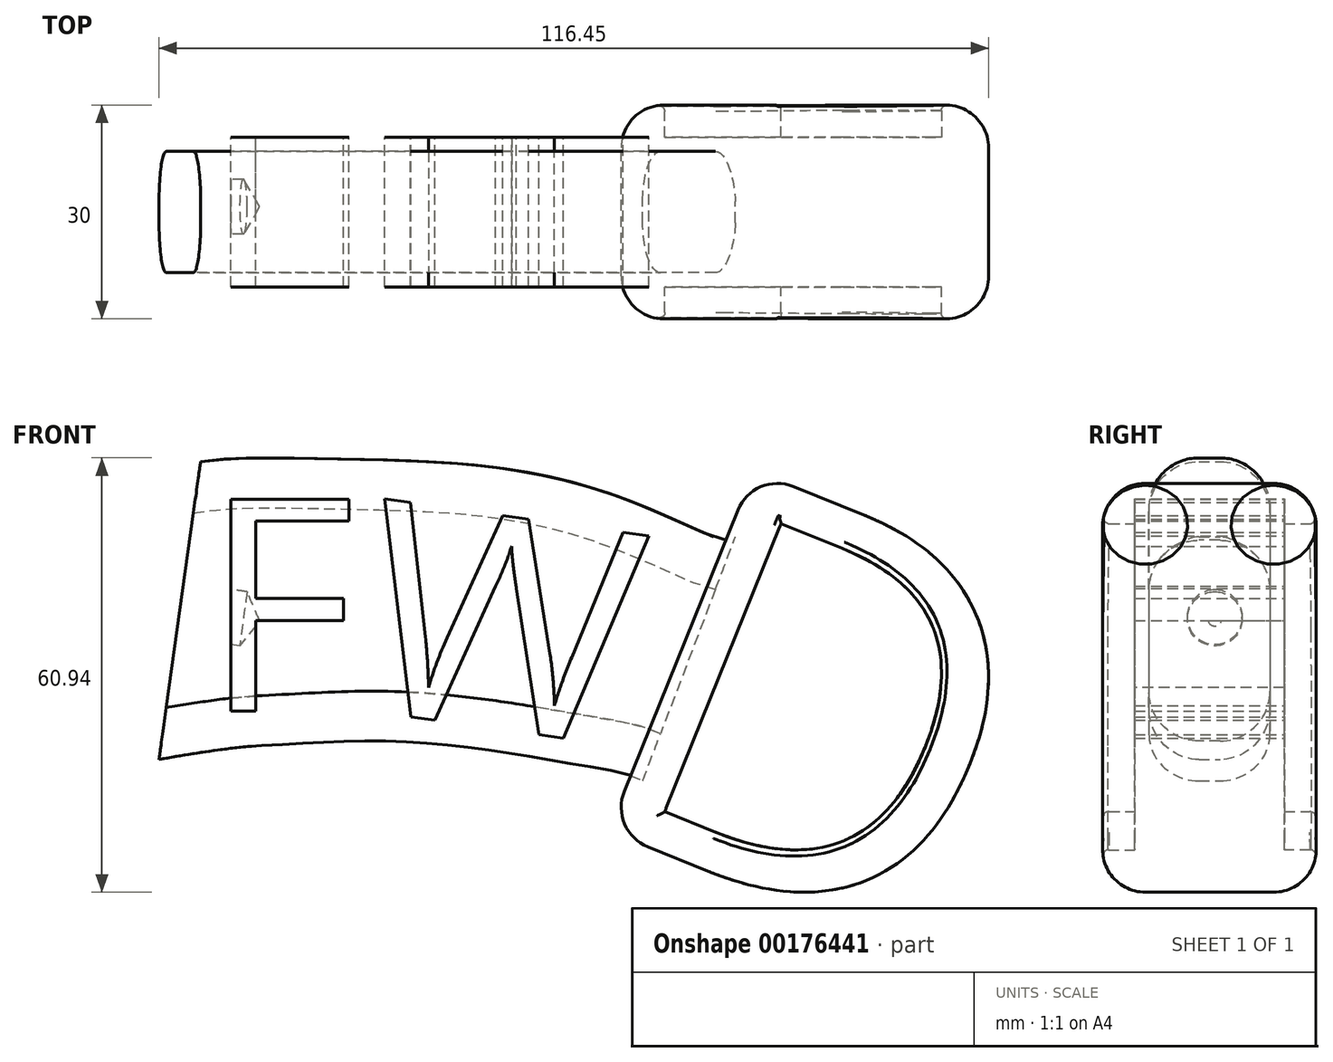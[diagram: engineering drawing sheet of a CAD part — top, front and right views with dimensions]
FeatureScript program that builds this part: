
annotation { "Feature Type Name" : "Feature", "Feature Type Description" : "" }
export const myFeature = defineFeature(function(context is Context, id is Id, definition is map)
    precondition{}
    {
        {
            var Q0;
            Q0=qCreatedBy(makeId("Front.planeOp"),FACE);
            var sketch = newSketch(context, id + "F0", { "sketchPlane" : qUnion([Q0])});
            skText(sketch, "E0", { "text": "F", "fontName": "OpenSans-Regular.ttf"});
            skText(sketch, "E1", { "text": "D", "fontName": "OpenSans-Regular.ttf"});
            skLineSegment(sketch, "E2", {"start": v(0, 30) * mm, "end": v(0, 0) * mm});
            skText(sketch, "E3", { "text": "W", "fontName": "OpenSans-Regular.ttf"});
            const initialGuessF0  = {"E0": [0, 0, 1, 0, 0.03], "E1": [0.08306, -0.01421, 1, 0, 0.055], "E3": [0.03928, 0, 1, 0, 0.03]};
            skSetInitialGuess(sketch, initialGuessF0);
            skSolve(sketch);
        }
        {
            var Q0;
            Q0=makeQuery(id+"F0.imprint","IMPRINT",FACE,{"disambiguationData":[TD([[makeQuery(id+"F0.imprint","IMPRINT",EDGE,{"derivedFrom":sQuery(id+"F0.wireOp",EDGE,"E3.sketch_text.stroke-0")}),-1.0]])]});
            var Q1;
            Q1=makeQuery(id+"F0.imprint","IMPRINT",FACE,{"disambiguationData":[TD([[makeQuery(id+"F0.imprint","IMPRINT",EDGE,{"derivedFrom":sQuery(id+"F0.wireOp",EDGE,"E0.sketch_text.stroke-0")}),-1.0]])]});
            extrude(context, id + "F1", {"entities" : qUnion([Q0, Q1]), "endBound" : BoundingType.SYMMETRIC, "depth" : 21 * mm});
        }
        {
            var Q0;
            Q0=makeQuery(id+"F0.imprint","IMPRINT",FACE,{"disambiguationData":[TD([[makeQuery(id+"F0.imprint","IMPRINT",EDGE,{"derivedFrom":sQuery(id+"F0.wireOp",EDGE,"E1.sketch_text.stroke-0")}),-1.0]])]});
            extrude(context, id + "F2", {"entities" : qUnion([Q0]), "endBound" : BoundingType.SYMMETRIC, "depth" : 30 * mm});
        }
        {
            var Q0;
            Q0=makeQuery(id+"F0.imprint","IMPRINT",FACE,{"disambiguationData":[TD([[makeQuery(id+"F0.imprint","IMPRINT",EDGE,{"derivedFrom":sQuery(id+"F0.wireOp",EDGE,"E1.sketch_text.stroke-7")}),1.0]])]});
            extrude(context, id + "F3", {"entities" : qUnion([Q0]), "operationType" : NewBodyOperationType.ADD, "endBound" : BoundingType.SYMMETRIC, "depth" : 21 * mm});
        }
        {
            var Q0;
            Q0=makeQuery(id+"F1.opExtrude","SWEPT_BODY",BODY,{"disambiguationData":[OSD([sQuery(id+"F0.wireOp",EDGE,"E3.sketch_text.stroke-0"),sQuery(id+"F0.wireOp",EDGE,"E3.sketch_text.stroke-1"),sQuery(id+"F0.wireOp",EDGE,"E3.sketch_text.stroke-2"),sQuery(id+"F0.wireOp",EDGE,"E3.sketch_text.stroke-3"),sQuery(id+"F0.wireOp",EDGE,"E3.sketch_text.stroke-4"),sQuery(id+"F0.wireOp",EDGE,"E3.sketch_text.stroke-5"),sQuery(id+"F0.wireOp",EDGE,"E3.sketch_text.stroke-6"),sQuery(id+"F0.wireOp",EDGE,"E3.sketch_text.stroke-7"),sQuery(id+"F0.wireOp",EDGE,"E3.sketch_text.stroke-8"),sQuery(id+"F0.wireOp",EDGE,"E3.sketch_text.stroke-9"),sQuery(id+"F0.wireOp",EDGE,"E3.sketch_text.stroke-10"),sQuery(id+"F0.wireOp",EDGE,"E3.sketch_text.stroke-11"),sQuery(id+"F0.wireOp",EDGE,"E3.sketch_text.stroke-12"),sQuery(id+"F0.wireOp",EDGE,"E3.sketch_text.stroke-13"),sQuery(id+"F0.wireOp",EDGE,"E3.sketch_text.stroke-14"),sQuery(id+"F0.wireOp",EDGE,"E3.sketch_text.stroke-15"),sQuery(id+"F0.wireOp",EDGE,"E3.sketch_text.stroke-16"),sQuery(id+"F0.wireOp",EDGE,"E3.sketch_text.stroke-17"),sQuery(id+"F0.wireOp",EDGE,"E3.sketch_text.stroke-18"),sQuery(id+"F0.wireOp",EDGE,"E3.sketch_text.stroke-19")])]});
            var Q1;
            Q1=makeQuery(id+"F1.opExtrude","SWEPT_EDGE",EDGE,{"disambiguationData":[OSD([sQuery(id+"F0.wireOp",EDGE,"E3.sketch_text.stroke-6"),sQuery(id+"F0.wireOp",EDGE,"E3.sketch_text.stroke-7")])]});
            transform(context, id + "F4", {"entities" : qUnion([Q0]), "transformType" : TransformType.ROTATION, "transformAxis" : qUnion([Q1]), "angle" : 8 * degree, "makeCopy" : false});
        }
        {
            var Q0;
            Q0=makeQuery(id+"F2.opExtrude","SWEPT_BODY",BODY,{"disambiguationData":[OSD([sQuery(id+"F0.wireOp",EDGE,"E1.sketch_text.stroke-0"),sQuery(id+"F0.wireOp",EDGE,"E1.sketch_text.stroke-1"),sQuery(id+"F0.wireOp",EDGE,"E1.sketch_text.stroke-2"),sQuery(id+"F0.wireOp",EDGE,"E1.sketch_text.stroke-3"),sQuery(id+"F0.wireOp",EDGE,"E1.sketch_text.stroke-4"),sQuery(id+"F0.wireOp",EDGE,"E1.sketch_text.stroke-5"),sQuery(id+"F0.wireOp",EDGE,"E1.sketch_text.stroke-6"),sQuery(id+"F0.wireOp",EDGE,"E1.sketch_text.stroke-7"),sQuery(id+"F0.wireOp",EDGE,"E1.sketch_text.stroke-8"),sQuery(id+"F0.wireOp",EDGE,"E1.sketch_text.stroke-9"),sQuery(id+"F0.wireOp",EDGE,"E1.sketch_text.stroke-10"),sQuery(id+"F0.wireOp",EDGE,"E1.sketch_text.stroke-11"),sQuery(id+"F0.wireOp",EDGE,"E1.sketch_text.stroke-12"),sQuery(id+"F0.wireOp",EDGE,"E1.sketch_text.stroke-13")])]});
            var Q1;
            Q1=makeQuery(id+"F2.opExtrude","SWEPT_EDGE",EDGE,{"disambiguationData":[OSD([sQuery(id+"F0.wireOp",EDGE,"E1.sketch_text.stroke-2"),sQuery(id+"F0.wireOp",EDGE,"E1.sketch_text.stroke-3")])]});
            transform(context, id + "F5", {"entities" : qUnion([Q0]), "transformType" : TransformType.ROTATION, "transformAxis" : qUnion([Q1]), "angle" : 22 * degree, "makeCopy" : false});
        }
        {
            var Q0;
            Q0=makeQuery(id+"F1.opExtrude","SWEPT_BODY",BODY,{"disambiguationData":[OSD([sQuery(id+"F0.wireOp",EDGE,"E3.sketch_text.stroke-0"),sQuery(id+"F0.wireOp",EDGE,"E3.sketch_text.stroke-1"),sQuery(id+"F0.wireOp",EDGE,"E3.sketch_text.stroke-2"),sQuery(id+"F0.wireOp",EDGE,"E3.sketch_text.stroke-3"),sQuery(id+"F0.wireOp",EDGE,"E3.sketch_text.stroke-4"),sQuery(id+"F0.wireOp",EDGE,"E3.sketch_text.stroke-5"),sQuery(id+"F0.wireOp",EDGE,"E3.sketch_text.stroke-6"),sQuery(id+"F0.wireOp",EDGE,"E3.sketch_text.stroke-7"),sQuery(id+"F0.wireOp",EDGE,"E3.sketch_text.stroke-8"),sQuery(id+"F0.wireOp",EDGE,"E3.sketch_text.stroke-9"),sQuery(id+"F0.wireOp",EDGE,"E3.sketch_text.stroke-10"),sQuery(id+"F0.wireOp",EDGE,"E3.sketch_text.stroke-11"),sQuery(id+"F0.wireOp",EDGE,"E3.sketch_text.stroke-12"),sQuery(id+"F0.wireOp",EDGE,"E3.sketch_text.stroke-13"),sQuery(id+"F0.wireOp",EDGE,"E3.sketch_text.stroke-14"),sQuery(id+"F0.wireOp",EDGE,"E3.sketch_text.stroke-15"),sQuery(id+"F0.wireOp",EDGE,"E3.sketch_text.stroke-16"),sQuery(id+"F0.wireOp",EDGE,"E3.sketch_text.stroke-17"),sQuery(id+"F0.wireOp",EDGE,"E3.sketch_text.stroke-18"),sQuery(id+"F0.wireOp",EDGE,"E3.sketch_text.stroke-19")])]});
            transform(context, id + "F6", {"entities" : qUnion([Q0]), "transformType" : TransformType.TRANSLATION_3D, "dx" : -18.4 * mm, "dy" : 0 * mm, "dz" : -0.8 * mm, "makeCopy" : false});
        }
        {
            var Q0;
            Q0=makeQuery(id+"F2.opExtrude","SWEPT_BODY",BODY,{"disambiguationData":[OSD([sQuery(id+"F0.wireOp",EDGE,"E1.sketch_text.stroke-0"),sQuery(id+"F0.wireOp",EDGE,"E1.sketch_text.stroke-1"),sQuery(id+"F0.wireOp",EDGE,"E1.sketch_text.stroke-2"),sQuery(id+"F0.wireOp",EDGE,"E1.sketch_text.stroke-3"),sQuery(id+"F0.wireOp",EDGE,"E1.sketch_text.stroke-4"),sQuery(id+"F0.wireOp",EDGE,"E1.sketch_text.stroke-5"),sQuery(id+"F0.wireOp",EDGE,"E1.sketch_text.stroke-6"),sQuery(id+"F0.wireOp",EDGE,"E1.sketch_text.stroke-7"),sQuery(id+"F0.wireOp",EDGE,"E1.sketch_text.stroke-8"),sQuery(id+"F0.wireOp",EDGE,"E1.sketch_text.stroke-9"),sQuery(id+"F0.wireOp",EDGE,"E1.sketch_text.stroke-10"),sQuery(id+"F0.wireOp",EDGE,"E1.sketch_text.stroke-11"),sQuery(id+"F0.wireOp",EDGE,"E1.sketch_text.stroke-12"),sQuery(id+"F0.wireOp",EDGE,"E1.sketch_text.stroke-13")])]});
            transform(context, id + "F7", {"entities" : qUnion([Q0]), "transformType" : TransformType.TRANSLATION_3D, "dx" : -33.5 * mm, "dy" : 0 * mm, "dz" : -2.6 * mm, "makeCopy" : false});
        }
        {
            var Q0;
            Q0=qCreatedBy(makeId("Front.planeOp"),FACE);
            var sketch = newSketch(context, id + "F8", { "sketchPlane" : qUnion([Q0])});
            skFitSpline(sketch, "E4", {"points": [v(-6.76, 33.3) * mm, v(16.6, 35.42) * mm, v(37.62, 34.58) * mm, v(55.87, 30.97) * mm, v(70.28, 25.09) * mm, v(74.89, 24.43) * mm], "startDerivative": vector(71.46, 31.76) * mm, "endDerivative": vector(26.56, 26.35) * mm});
            skLineSegment(sketch, "E5", {"start": v(74.89, 24.43) * mm, "end": v(61.87, -9.78) * mm});
            skFitSpline(sketch, "E6", {"points": [v(61.87, -9.78) * mm, v(54.15, -7.78) * mm, v(40.45, -5.5) * mm, v(25.93, -4.22) * mm, v(15.32, -4.48) * mm, v(7.34, -4.9) * mm, v(0.8, -5.68) * mm, v(-16.3, -9.78) * mm], "startDerivative": vector(-38.1, 25.6) * mm, "endDerivative": vector(-38.62, -30.25) * mm});
            skLineSegment(sketch, "E7", {"start": v(0, 36.27) * mm, "end": v(-6.32, -8.97) * mm});
            skSolve(sketch);
        }
        {
            var Q0;
            Q0=makeQuery(id+"F8.imprint","IMPRINT",FACE,{"disambiguationData":[TD([[makeQuery(id+"F8.imprint","IMPRINT",EDGE,{"derivedFrom":sQuery(id+"F8.wireOp",EDGE,"E4")}),-1.0]])]});
            extrude(context, id + "F9", {"entities" : qUnion([Q0]), "endBound" : BoundingType.SYMMETRIC, "depth" : 17 * mm});
        }
        {
            var Q0;
            Q0=makeQuery(id+"F9.opExtrude","CAP_EDGE",EDGE,{"disambiguationData":[OSD([sQuery(id+"F8.wireOp",EDGE,"E4")])],"isStart":false});
            var Q1;
            Q1=makeQuery(id+"F9.opExtrude","CAP_EDGE",EDGE,{"disambiguationData":[OSD([sQuery(id+"F8.wireOp",EDGE,"E4")])],"isStart":true});
            var Q2;
            Q2=makeQuery(id+"F9.opExtrude","CAP_EDGE",EDGE,{"disambiguationData":[OSD([sQuery(id+"F8.wireOp",EDGE,"dd5d9441-1a1e-4af7-8796-b4c284a6af80")])],"isStart":false});
            var Q3;
            Q3=makeQuery(id+"F9.opExtrude","CAP_EDGE",EDGE,{"disambiguationData":[OSD([sQuery(id+"F8.wireOp",EDGE,"dd5d9441-1a1e-4af7-8796-b4c284a6af80")])],"isStart":true});
            var Q4;
            Q4=makeQuery(id+"F9.opExtrude","CAP_EDGE",EDGE,{"disambiguationData":[OSD([sQuery(id+"F8.wireOp",EDGE,"E6")])],"isStart":false});
            var Q5;
            Q5=makeQuery(id+"F9.opExtrude","CAP_EDGE",EDGE,{"disambiguationData":[OSD([sQuery(id+"F8.wireOp",EDGE,"E6")])],"isStart":true});
            fillet(context, id + "F10", {"entities" : qUnion([Q0, Q1, Q2, Q3, Q4, Q5]), "radius" : 7 * mm, "tangentPropagation" : true, "allowEdgeOverflow" : false});
        }
        {
            var Q0;
            Q0=makeQuery(id+"F2.opExtrude","CAP_EDGE",EDGE,{"disambiguationData":[OSD([sQuery(id+"F0.wireOp",EDGE,"E1.sketch_text.stroke-1")])],"isStart":false});
            var Q1;
            Q1=makeQuery(id+"F2.opExtrude","CAP_EDGE",EDGE,{"disambiguationData":[OSD([sQuery(id+"F0.wireOp",EDGE,"E1.sketch_text.stroke-1")])],"isStart":true});
            var Q2;
            Q2=makeQuery(id+"F2.opExtrude","CAP_EDGE",EDGE,{"disambiguationData":[OSD([sQuery(id+"F0.wireOp",EDGE,"E1.sketch_text.stroke-3")])],"isStart":false});
            var Q3;
            Q3=makeQuery(id+"F2.opExtrude","SWEPT_EDGE",EDGE,{"disambiguationData":[OSD([sQuery(id+"F0.wireOp",EDGE,"E1.sketch_text.stroke-2"),sQuery(id+"F0.wireOp",EDGE,"E1.sketch_text.stroke-3")])]});
            var Q4;
            Q4=makeQuery(id+"F2.opExtrude","CAP_EDGE",EDGE,{"disambiguationData":[OSD([sQuery(id+"F0.wireOp",EDGE,"E1.sketch_text.stroke-3")])],"isStart":true});
            var Q5;
            Q5=makeQuery(id+"F2.opExtrude","SWEPT_EDGE",EDGE,{"disambiguationData":[OSD([sQuery(id+"F0.wireOp",EDGE,"E1.sketch_text.stroke-3"),sQuery(id+"F0.wireOp",EDGE,"E1.sketch_text.stroke-4")])]});
            fillet(context, id + "F11", {"entities" : qUnion([Q0, Q1, Q2, Q3, Q4, Q5]), "radius" : 6 * mm, "tangentPropagation" : true, "allowEdgeOverflow" : false});
        }
        {
            var Q0;
            Q0=makeQuery(id+"F9.opExtrude","SWEPT_FACE",FACE,{"disambiguationData":[OSD([sQuery(id+"F8.wireOp",EDGE,"E7")])]});
            var sketch = newSketch(context, id + "F12", { "sketchPlane" : qUnion([Q0])});
            skLineSegment(sketch, "E8", {"start": v(0, 33.84) * mm, "end": v(0, 33.84) * mm});
            skLineSegment(sketch, "E9", {"start": v(0, 33.84) * mm, "end": v(-1.5, -6.57) * mm, "construction": true});
            skPoint(sketch, "E10", {"position": v(-0.75, 13.64) * mm});
            skSolve(sketch);
        }
        {
            var Q0;
            Q0=sQuery(id+"F12.wireOp",VERTEX,"E10");
            var Q1;
            Q1=makeQuery(id+"F1.opExtrude","SWEPT_BODY",BODY,{"disambiguationData":[OSD([sQuery(id+"F0.wireOp",EDGE,"E0.sketch_text.stroke-0"),sQuery(id+"F0.wireOp",EDGE,"E0.sketch_text.stroke-1"),sQuery(id+"F0.wireOp",EDGE,"E0.sketch_text.stroke-2"),sQuery(id+"F0.wireOp",EDGE,"E0.sketch_text.stroke-3"),sQuery(id+"F0.wireOp",EDGE,"E0.sketch_text.stroke-4"),sQuery(id+"F0.wireOp",EDGE,"E0.sketch_text.stroke-5"),sQuery(id+"F0.wireOp",EDGE,"E0.sketch_text.stroke-6"),sQuery(id+"F0.wireOp",EDGE,"E0.sketch_text.stroke-7"),sQuery(id+"F0.wireOp",EDGE,"E0.sketch_text.stroke-8"),sQuery(id+"F0.wireOp",EDGE,"E0.sketch_text.stroke-9")])]});
            hole(context, id + "F13", {"style" : HoleStyle.C_SINK, "endStyle" : HoleEndStyle.BLIND, "holeDiameter" : 7.67 * mm, "cSinkDiameter" : 9 * mm, "cSinkAngle" : 83 * degree, "holeDepth" : 9 * mm, "startFromSketch" : true, "locations" : qUnion([Q0]), "scope" : qUnion([Q1])});
        }
        {
            var Q0;
            {var subQ0=sQuery(id+"F0.wireOp",EDGE,"E1.sketch_text.stroke-13");var subQ1=sQuery(id+"F0.wireOp",EDGE,"E1.sketch_text.stroke-12");var subQ2=sQuery(id+"F0.wireOp",EDGE,"E1.sketch_text.stroke-11");var subQ3=sQuery(id+"F0.wireOp",EDGE,"E1.sketch_text.stroke-10");var subQ4=sQuery(id+"F0.wireOp",EDGE,"E1.sketch_text.stroke-9");var subQ5=sQuery(id+"F0.wireOp",EDGE,"E1.sketch_text.stroke-8");var subQ6=sQuery(id+"F0.wireOp",EDGE,"E1.sketch_text.stroke-7");var subQ7=sQuery(id+"F0.wireOp",EDGE,"E1.sketch_text.stroke-2");Q0=makeQuery(id+"F11.opFillet","BLEND_EDGE",EDGE,{"blendedFrom":[makeQuery(id+"F2.opExtrude","CAP_EDGE",EDGE,{"disambiguationData":[OSD([subQ7])],"isStart":false}),makeQuery(id+"F3.boolean.opBoolean","SPLIT",FACE,{"disambiguationData":[TD([makeQuery(id+"F3.opExtrude","CAP_FACE",FACE,{"disambiguationData":[OSD([subQ6,subQ5,subQ4,subQ3,subQ2,subQ1,subQ0])],"isStart":false})])],"derivedFrom":makeQuery(id+"F2.opExtrude","SWEPT_FACE",FACE,{"disambiguationData":[OSD([subQ2])]})})],"blendedInto":[makeQuery(id+"F3.boolean.opBoolean","SPLIT",FACE,{"disambiguationData":[TD([makeQuery(id+"F3.opExtrude","CAP_FACE",FACE,{"disambiguationData":[OSD([subQ6,subQ5,subQ4,subQ3,subQ2,subQ1,subQ0])],"isStart":false})])],"derivedFrom":makeQuery(id+"F2.opExtrude","SWEPT_FACE",FACE,{"disambiguationData":[OSD([subQ2])]})})]});}
            var Q1;
            Q1=makeQuery(id+"F2.opExtrude","CAP_EDGE",EDGE,{"disambiguationData":[OSD([sQuery(id+"F0.wireOp",EDGE,"E1.sketch_text.stroke-10")])],"isStart":false});
            var Q2;
            Q2=makeQuery(id+"F2.opExtrude","CAP_EDGE",EDGE,{"disambiguationData":[OSD([sQuery(id+"F0.wireOp",EDGE,"E1.sketch_text.stroke-13")])],"isStart":true});
            var Q3;
            Q3=makeQuery(id+"F2.opExtrude","CAP_EDGE",EDGE,{"disambiguationData":[OSD([sQuery(id+"F0.wireOp",EDGE,"E1.sketch_text.stroke-10")])],"isStart":true});
            fillet(context, id + "F14", {"entities" : qUnion([Q0, Q1, Q2, Q3]), "radius" : .75 * mm, "tangentPropagation" : true, "allowEdgeOverflow" : false});
        }
    });
